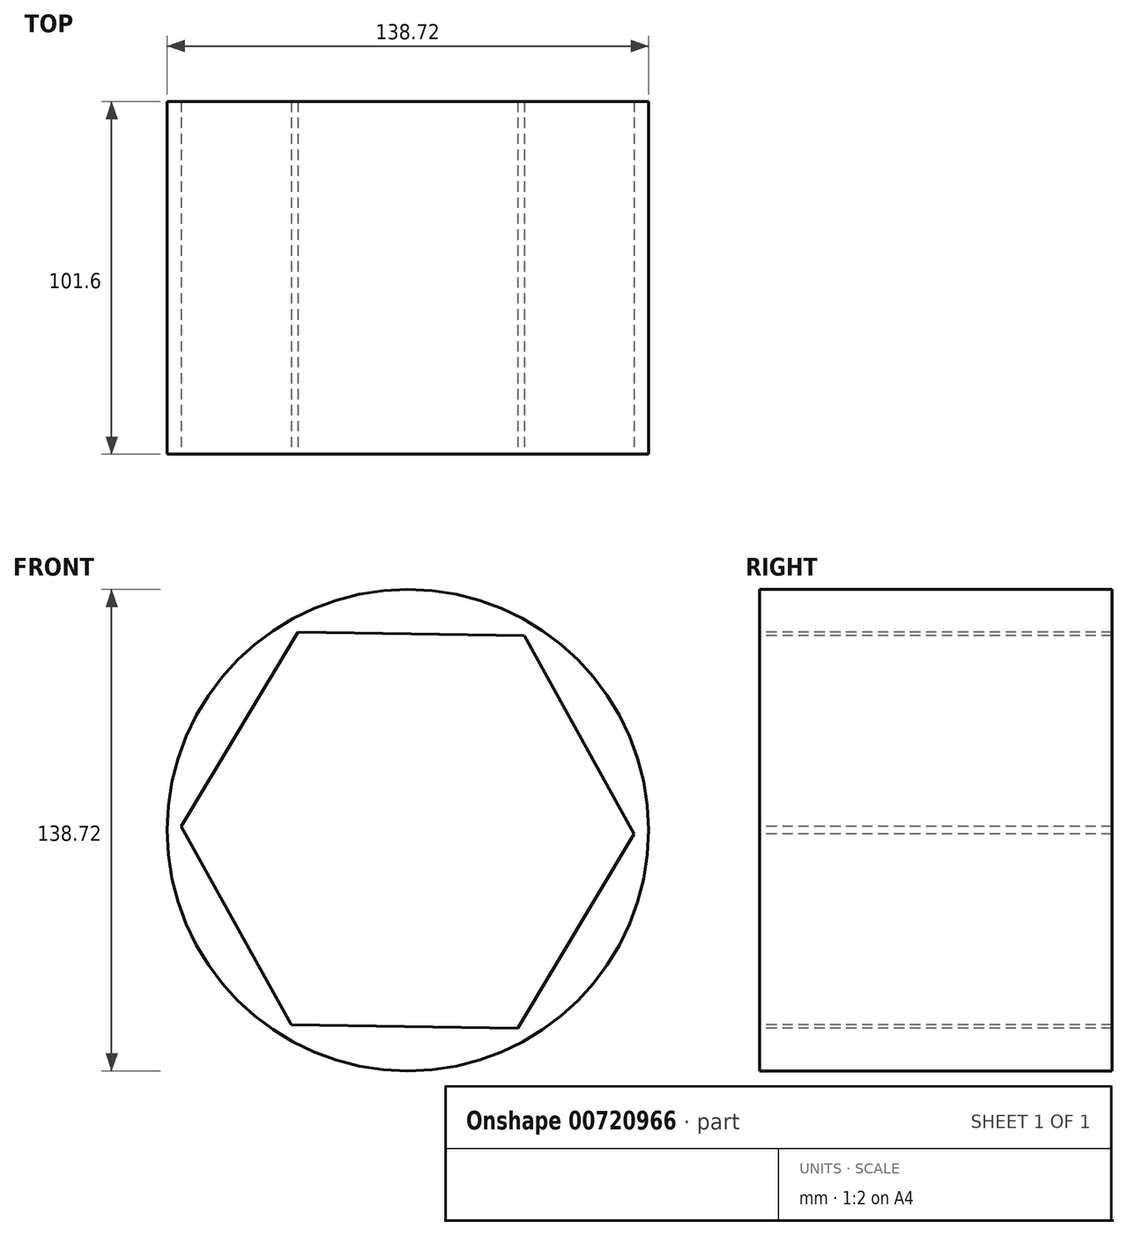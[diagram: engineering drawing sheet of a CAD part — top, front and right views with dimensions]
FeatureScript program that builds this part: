
annotation { "Feature Type Name" : "Feature", "Feature Type Description" : "" }
export const myFeature = defineFeature(function(context is Context, id is Id, definition is map)
    precondition{}
    {
        {
            var Q0;
            Q0=qCreatedBy(makeId("Front.planeOp"),FACE);
            var sketch = newSketch(context, id + "F0", { "sketchPlane" : qUnion([Q0])});
            skCircle(sketch, "E0", {"center": v(0, 0) * mm, "radius": 69.36 * mm});
            skCircle(sketch, "E1.cCircle", {"center": v(0, 0) * mm, "radius": 65.29 * mm, "construction": true});
            skLineSegment(sketch, "E1.0", {"start": v(33.54, 56.01) * mm, "end": v(65.28, -1.04) * mm});
            skLineSegment(sketch, "E1.1", {"start": v(65.28, -1.04) * mm, "end": v(31.74, -57.05) * mm});
            skLineSegment(sketch, "E1.2", {"start": v(31.74, -57.05) * mm, "end": v(-33.54, -56.01) * mm});
            skLineSegment(sketch, "E1.3", {"start": v(-33.54, -56.01) * mm, "end": v(-65.28, 1.04) * mm});
            skLineSegment(sketch, "E1.4", {"start": v(-65.28, 1.04) * mm, "end": v(-31.74, 57.05) * mm});
            skLineSegment(sketch, "E1.5", {"start": v(-31.74, 57.05) * mm, "end": v(33.54, 56.01) * mm});
            skSolve(sketch);
        }
        {
            var Q0;
            Q0=makeQuery(id+"F0.imprint","IMPRINT",FACE,{"disambiguationData":[TD([[makeQuery(id+"F0.imprint","IMPRINT",EDGE,{"derivedFrom":sQuery(id+"F0.wireOp",EDGE,"E0")}),1.0]])]});
            extrude(context, id + "F1", {"entities" : qUnion([Q0]), "oppositeDirection" : true, "depth" : 101.6 * mm, "offsetDistance" : 25.4 * mm});
        }
    });
